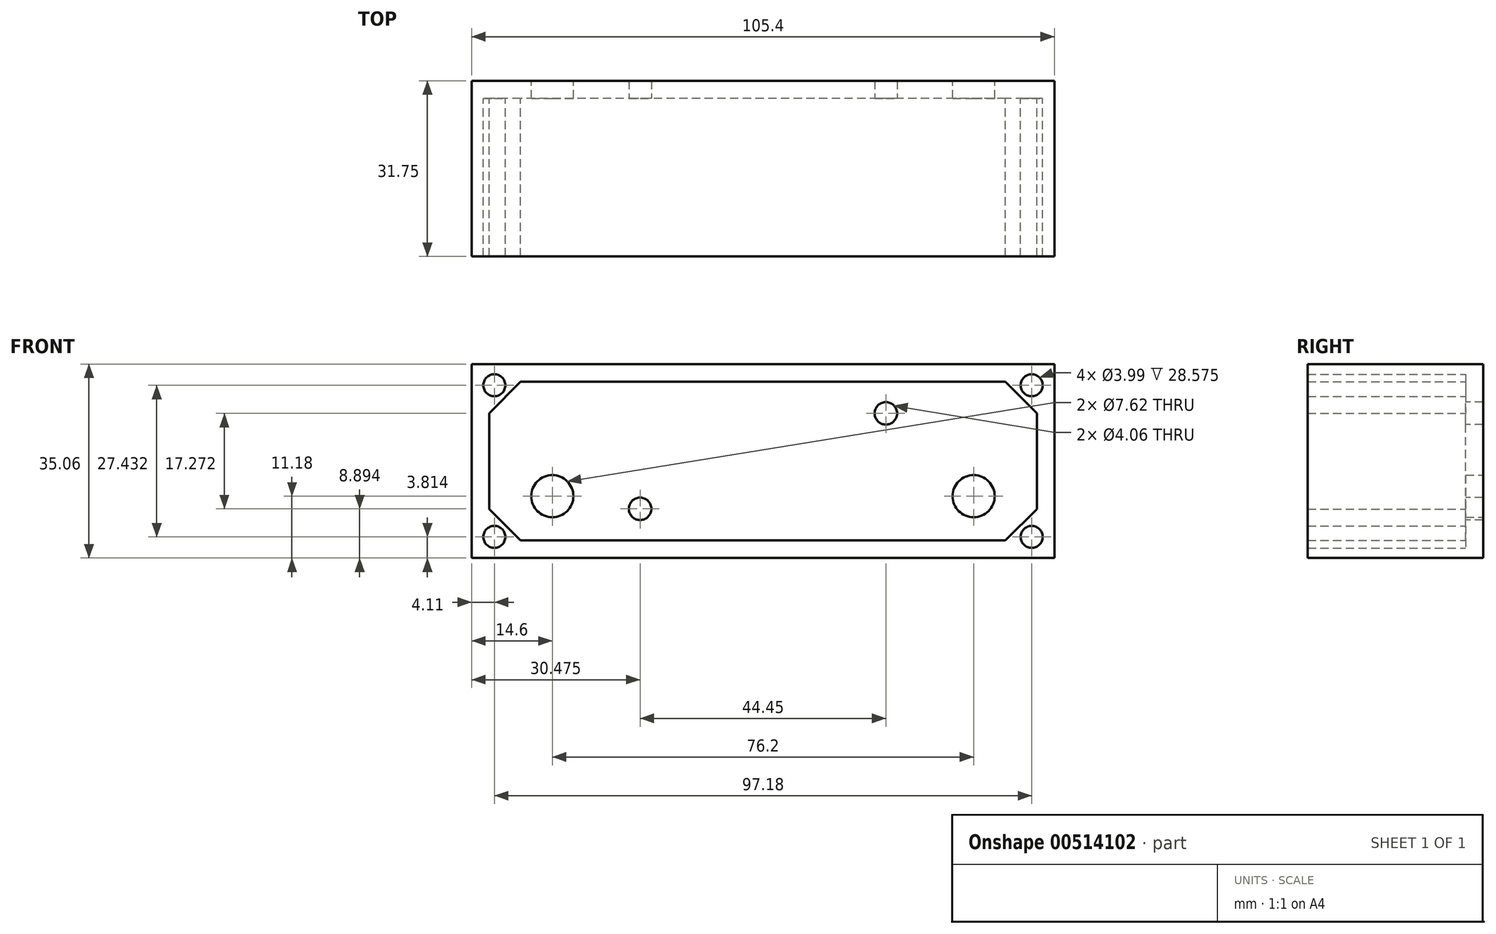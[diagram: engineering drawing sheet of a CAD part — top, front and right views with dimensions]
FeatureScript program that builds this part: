
annotation { "Feature Type Name" : "Feature", "Feature Type Description" : "" }
export const myFeature = defineFeature(function(context is Context, id is Id, definition is map)
    precondition{}
    {
        {
            var Q0;
            Q0=qCreatedBy(makeId("Front.planeOp"),FACE);
            var sketch = newSketch(context, id + "F0", { "sketchPlane" : qUnion([Q0])});
            skLineSegment(sketch, "E0.bottom", {"start": v(52.7, 17.53) * mm, "end": v(-52.7, 17.53) * mm});
            skLineSegment(sketch, "E0.top", {"start": v(52.7, -17.53) * mm, "end": v(-52.7, -17.53) * mm});
            skLineSegment(sketch, "E0.left", {"start": v(52.7, 17.53) * mm, "end": v(52.7, -17.53) * mm});
            skLineSegment(sketch, "E0.right", {"start": v(-52.7, 17.53) * mm, "end": v(-52.7, -17.53) * mm});
            skPoint(sketch, "E0.middle", {"position": v(0, 0) * mm});
            skCircle(sketch, "E1", {"center": v(-48.6, -13.72) * mm, "radius": 2 * mm});
            skCircle(sketch, "E2", {"center": v(-48.6, 13.72) * mm, "radius": 2 * mm});
            skCircle(sketch, "E3", {"center": v(-38.1, -6.35) * mm, "radius": 3.81 * mm});
            skCircle(sketch, "E4", {"center": v(38.1, -6.35) * mm, "radius": 3.81 * mm});
            skLineSegment(sketch, "E5", {"start": v(-49.53, 8.66) * mm, "end": v(-43.84, 14.35) * mm, "construction": true});
            skLineSegment(sketch, "E6.MirrorCS", {"start": v(-49.53, -8.66) * mm, "end": v(-43.84, -14.35) * mm, "construction": true});
            skLineSegment(sketch, "E7.MirrorCS", {"start": v(49.53, 8.66) * mm, "end": v(43.84, 14.35) * mm, "construction": true});
            skLineSegment(sketch, "E8.MirrorCS", {"start": v(49.53, -8.66) * mm, "end": v(43.84, -14.35) * mm, "construction": true});
            skLineSegment(sketch, "E9", {"start": v(-49.53, 8.66) * mm, "end": v(-43.84, 14.35) * mm});
            skLineSegment(sketch, "E10", {"start": v(43.84, 14.35) * mm, "end": v(49.53, 8.66) * mm});
            skLineSegment(sketch, "E11", {"start": v(49.53, -8.66) * mm, "end": v(43.84, -14.35) * mm});
            skLineSegment(sketch, "E12", {"start": v(-43.84, -14.35) * mm, "end": v(-49.53, -8.66) * mm});
            skLineSegment(sketch, "E13", {"start": v(-49.53, -8.66) * mm, "end": v(-49.53, 8.66) * mm});
            skLineSegment(sketch, "E14", {"start": v(-43.84, 14.35) * mm, "end": v(43.84, 14.35) * mm});
            skLineSegment(sketch, "E15", {"start": v(49.53, 8.66) * mm, "end": v(49.53, -8.66) * mm});
            skLineSegment(sketch, "E16", {"start": v(43.84, -14.35) * mm, "end": v(-43.84, -14.35) * mm});
            skCircle(sketch, "E17.MirrorC", {"center": v(48.6, 13.72) * mm, "radius": 2 * mm});
            skCircle(sketch, "E18.MirrorC", {"center": v(48.6, -13.72) * mm, "radius": 2 * mm});
            skSolve(sketch);
        }
        {
            var Q0;
            Q0 = qSketchRegion(id + "F0", true);
            extrude(context, id + "F1", {"entities" : qUnion([Q0]), "depth" : 31.75 * mm, "offsetDistance" : 25.4 * mm});
        }
        {
            var Q0;
            Q0=makeQuery(id+"F1.opExtrude","CAP_FACE",FACE,{"disambiguationData":[OSD([sQuery(id+"F0.wireOp",EDGE,"E0.bottom"),sQuery(id+"F0.wireOp",EDGE,"E0.top"),sQuery(id+"F0.wireOp",EDGE,"E0.left"),sQuery(id+"F0.wireOp",EDGE,"E0.right"),sQuery(id+"F0.wireOp",EDGE,"E1"),sQuery(id+"F0.wireOp",EDGE,"E2"),sQuery(id+"F0.wireOp",EDGE,"E9"),sQuery(id+"F0.wireOp",EDGE,"E10"),sQuery(id+"F0.wireOp",EDGE,"E11"),sQuery(id+"F0.wireOp",EDGE,"E12"),sQuery(id+"F0.wireOp",EDGE,"E13"),sQuery(id+"F0.wireOp",EDGE,"E14"),sQuery(id+"F0.wireOp",EDGE,"E15"),sQuery(id+"F0.wireOp",EDGE,"E16"),sQuery(id+"F0.wireOp",EDGE,"E17.MirrorC"),sQuery(id+"F0.wireOp",EDGE,"E18.MirrorC")])],"isStart":true});
            var sketch = newSketch(context, id + "F2", { "sketchPlane" : qUnion([Q0])});
            skLineSegment(sketch, "E19.bottom", {"start": v(-52.7, 17.53) * mm, "end": v(52.7, 17.53) * mm});
            skLineSegment(sketch, "E19.top", {"start": v(-52.7, -17.53) * mm, "end": v(52.7, -17.53) * mm});
            skLineSegment(sketch, "E19.left", {"start": v(-52.7, 17.53) * mm, "end": v(-52.7, -17.53) * mm});
            skLineSegment(sketch, "E19.right", {"start": v(52.7, 17.53) * mm, "end": v(52.7, -17.53) * mm});
            skSolve(sketch);
        }
        {
            var Q0;
            Q0 = qSketchRegion(id + "F2", true);
            extrude(context, id + "F3", {"entities" : qUnion([Q0]), "operationType" : NewBodyOperationType.ADD, "oppositeDirection" : true, "depth" : 3.17 * mm});
        }
        {
            var Q0;
            Q0=makeQuery(id+"F3.boolean.opBoolean","MERGE",FACE,{"derivedFrom":[makeQuery(id+"F1.opExtrude","CAP_FACE",FACE,{"disambiguationData":[OSD([sQuery(id+"F0.wireOp",EDGE,"E0.bottom"),sQuery(id+"F0.wireOp",EDGE,"E0.top"),sQuery(id+"F0.wireOp",EDGE,"E0.left"),sQuery(id+"F0.wireOp",EDGE,"E0.right"),sQuery(id+"F0.wireOp",EDGE,"E1"),sQuery(id+"F0.wireOp",EDGE,"E2"),sQuery(id+"F0.wireOp",EDGE,"E9"),sQuery(id+"F0.wireOp",EDGE,"E10"),sQuery(id+"F0.wireOp",EDGE,"E11"),sQuery(id+"F0.wireOp",EDGE,"E12"),sQuery(id+"F0.wireOp",EDGE,"E13"),sQuery(id+"F0.wireOp",EDGE,"E14"),sQuery(id+"F0.wireOp",EDGE,"E15"),sQuery(id+"F0.wireOp",EDGE,"E16"),sQuery(id+"F0.wireOp",EDGE,"E17.MirrorC"),sQuery(id+"F0.wireOp",EDGE,"E18.MirrorC")])],"isStart":true}),makeQuery(id+"F3.opExtrude","CAP_FACE",FACE,{"disambiguationData":[OSD([sQuery(id+"F2.wireOp",EDGE,"E19.bottom"),sQuery(id+"F2.wireOp",EDGE,"E19.top"),sQuery(id+"F2.wireOp",EDGE,"E19.left"),sQuery(id+"F2.wireOp",EDGE,"E19.right")])],"isStart":true})]});
            var sketch = newSketch(context, id + "F4", { "sketchPlane" : qUnion([Q0])});
            skCircle(sketch, "E20", {"center": v(-38.1, -6.35) * mm, "radius": 3.81 * mm});
            skCircle(sketch, "E21.MirrorC", {"center": v(38.1, -6.35) * mm, "radius": 3.81 * mm});
            skSolve(sketch);
        }
        {
            var Q0;
            Q0 = qSketchRegion(id + "F4", true);
            extrude(context, id + "F5", {"entities" : qUnion([Q0]), "operationType" : NewBodyOperationType.REMOVE, "oppositeDirection" : true, "depth" : 25.4 * mm});
        }
        {
            var Q0;
            Q0=makeQuery(id+"F3.boolean.opBoolean","SPLIT",FACE,{"disambiguationData":[TD([makeQuery(id+"F1.opExtrude","SWEPT_FACE",FACE,{"disambiguationData":[OSD([sQuery(id+"F0.wireOp",EDGE,"E9")])]})])],"derivedFrom":makeQuery(id+"F3.opExtrude","CAP_FACE",FACE,{"disambiguationData":[OSD([sQuery(id+"F2.wireOp",EDGE,"E19.bottom"),sQuery(id+"F2.wireOp",EDGE,"E19.top"),sQuery(id+"F2.wireOp",EDGE,"E19.left"),sQuery(id+"F2.wireOp",EDGE,"E19.right")])],"isStart":false})});
            var sketch = newSketch(context, id + "F6", { "sketchPlane" : qUnion([Q0])});
            skCircle(sketch, "E22", {"center": v(-22.23, 8.64) * mm, "radius": 2.03 * mm, "construction": true});
            skCircle(sketch, "E23.MirrorC", {"center": v(-22.23, -8.64) * mm, "radius": 2.03 * mm, "construction": true});
            skCircle(sketch, "E24.MirrorC", {"center": v(22.23, -8.64) * mm, "radius": 2.03 * mm, "construction": true});
            skCircle(sketch, "E25.MirrorC", {"center": v(22.23, 8.64) * mm, "radius": 2.03 * mm});
            skCircle(sketch, "E26.MirrorC", {"center": v(-22.23, -8.64) * mm, "radius": 2.03 * mm});
            skSolve(sketch);
        }
        {
            var Q0;
            Q0 = qSketchRegion(id + "F6", true);
            extrude(context, id + "F7", {"entities" : qUnion([Q0]), "operationType" : NewBodyOperationType.REMOVE, "oppositeDirection" : true, "depth" : 25.4 * mm});
        }
    });
